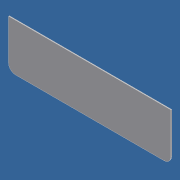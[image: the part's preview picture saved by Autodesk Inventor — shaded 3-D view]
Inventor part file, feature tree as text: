
AUTODESK INVENTOR PART (.ipt)
format: ipt  version: 2012 (Build 160160000, 160)  size: 70,656 bytes
history: native  units: in
note: dims shown in document units (in); Inventor stores cm internally (conversion verified against a paired STEP export)
features: extrude x1, fillet x1, sketch x1
ambient origin geometry x8: Origin, YZ Plane, XZ Plane, XY Plane, X Axis, Y Axis, Z Axis, Center Point
bodies: Solid1 (feature_tree)
feature tree (3):
  extrude  "Extrusion1"  Depth=14.0in
  fillet  "Fillet1"  Radius=0.25in
  sketch  "Sketch1"  dims[d0=48.0in d1=14.0in d2=0.25in d3=0.0in d4=2.0in]
